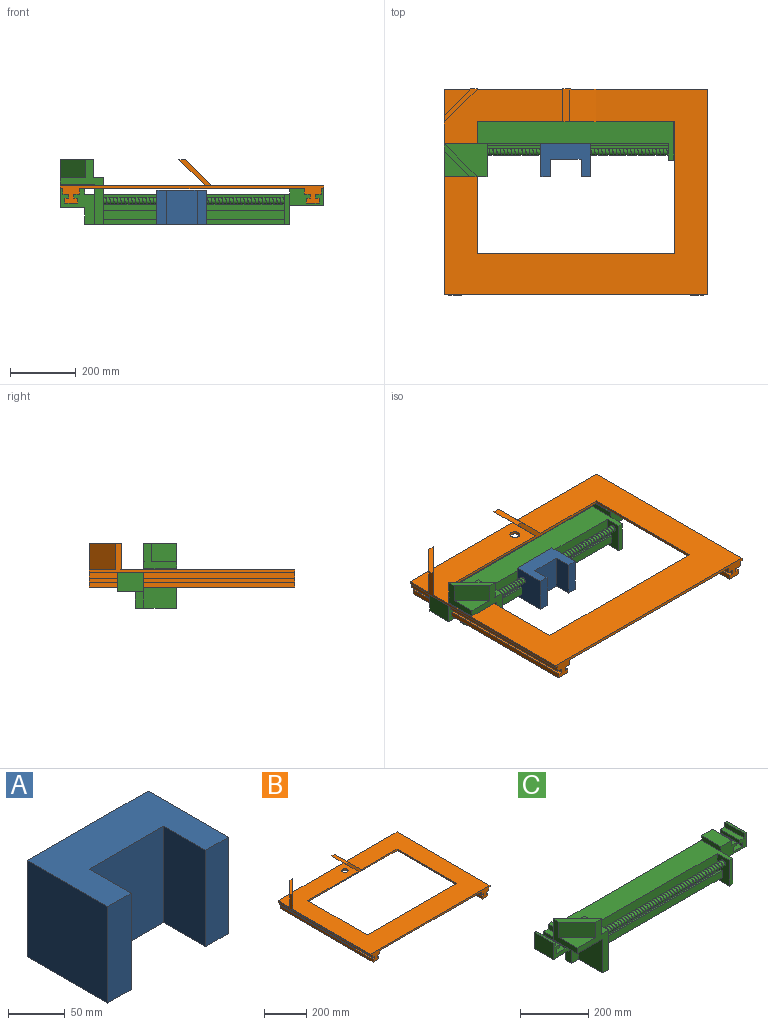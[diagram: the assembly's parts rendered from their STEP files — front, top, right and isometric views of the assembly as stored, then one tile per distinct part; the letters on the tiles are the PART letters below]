
ASSEMBLY  parts=3 mates=3
PART A: 10 faces, bbox 150x100x104 mm
  f0: plane 150x104mm, normal (0,1,0), area 15600mm2, adj f1,f7,f8,f9
  f1: plane 104x100mm, normal (1,0,0), area 10400mm2, adj f0,f2,f8,f9
  f2: plane 104x28.15mm, normal (0,-1,0), area 2927.1mm2, adj f1,f3,f8,f9
  f3: plane 104x52.39mm, normal (-1,0,0), area 5448.2mm2, adj f2,f4,f8,f9
  f4: plane 104x93.1mm, normal (0,-1,0), area 9682.7mm2, adj f3,f5,f8,f9
  f5: plane 104x52.39mm, normal (1,0,0), area 5448.2mm2, adj f4,f6,f8,f9
  f6: plane 104x28.75mm, normal (0,-1,0), area 2990.2mm2, adj f5,f7,f8,f9
  f7: plane 104x100mm, normal (-1,0,0), area 10400mm2, adj f0,f6,f8,f9
  f8: plane 150x100mm, normal (0,0,1), area 10122.7mm2, adj f0,f1,f2,f3,f4,f5,f6,f7
  f9: plane 150x100mm, normal (0,0,-1), area 10122.7mm2, adj f0,f1,f2,f3,f4,f5,f6,f7
PART B: 42 faces, bbox 800x625x132 mm
  f0: plane 625x7.98mm, normal (0,0,-1), area 4984.4mm2, adj f6,f8,f40,f41
  f1: plane 682.77x625mm, normal (0,0,-1), area 186024.3mm2, adj f3,f4,f5,f6,f9,f15,f29,f30
  f2: plane 800x625mm, normal (0,0,1), area 252293.1mm2, adj f3,f4,f5,f6,f7,f8,f9,f12
  f3: plane 600x88mm, normal (0,-1,0), area 6400mm2, adj f1,f2,f4,f9,f12,f13,f14
  f4: plane 400x8mm, normal (-1,0,0), area 3200mm2, adj f1,f2,f3,f5
  f5: plane 600x8mm, normal (0,1,0), area 4800mm2, adj f1,f2,f4,f9
  f6: plane 800x132mm, normal (0,1,0), area 12854.9mm2, adj f0,f1,f2,f7,f8,f10,f11,f12
  f7: plane 625x88mm, normal (-1,0,0), area 6600mm2, adj f2,f6,f10,f11,f16,f17,f18,f41
  f8: plane 625x8mm, normal (1,0,0), area 5000mm2, adj f0,f2,f6,f41
  f9: plane 400x8mm, normal (1,0,0), area 3200mm2, adj f1,f2,f3,f5
  f10: plane 80x80mm, normal (0,0,1), area 3200mm2, adj f6,f7,f16
  f11: plane 625x7.98mm, normal (0,0,-1), area 4984.4mm2, adj f6,f7,f19,f41
  f12: plane 100x80mm, normal (0.71,0,0.71), area 11313.7mm2, adj f2,f3,f6,f14
  f13: plane 100x80mm, normal (-0.71,0,-0.71), area 11313.7mm2, adj f2,f3,f6,f14
  f14: plane 100x20mm, normal (0,0,1), area 2000mm2, adj f3,f6,f12,f13
  f15: cylinder r=15mm len=30mm, axis (0,0,-1), area 754mm2, adj f1,f2
  f16: plane 80x80mm, normal (-0.71,0.71,0), area 9051mm2, adj f6,f7,f10,f18
  f17: plane 100x100mm, normal (0.71,-0.71,0), area 11313.7mm2, adj f2,f6,f7,f18
  f18: plane 100x100mm, normal (0,0,1), area 1800mm2, adj f6,f7,f16,f17
  f19: plane 625x17.11mm, normal (-1,0,0), area 10694.5mm2, adj f6,f11,f20,f41
  f20: plane 625x17.86mm, normal (0,0,-1), area 11162mm2, adj f6,f19,f21,f41
  f21: plane 625x12.04mm, normal (-1,0,0), area 7525mm2, adj f6,f20,f22,f41
  f22: plane 625x12.11mm, normal (0,0,1), area 7570.6mm2, adj f6,f21,f23,f41
  f23: plane 625x14.85mm, normal (-1,0,0), area 9280.6mm2, adj f6,f22,f24,f41
  f24: plane 625x39.15mm, normal (0,0,-1), area 24467.1mm2, adj f6,f23,f25,f41
  f25: plane 625x14.85mm, normal (1,0,0), area 9280.6mm2, adj f6,f24,f26,f41
  f26: plane 625x12.11mm, normal (0,0,1), area 7570.6mm2, adj f6,f25,f27,f41
  f27: plane 625x12.04mm, normal (1,0,0), area 7525mm2, adj f6,f26,f28,f41
  f28: plane 625x17.86mm, normal (0,0,-1), area 11162mm2, adj f6,f27,f29,f41
  f29: plane 625x17.11mm, normal (1,0,0), area 10694.5mm2, adj f1,f6,f28,f41
  f30: plane 625x17.11mm, normal (-1,0,0), area 10694.5mm2, adj f1,f6,f31,f41
  f31: plane 625x17.86mm, normal (0,0,-1), area 11162mm2, adj f6,f30,f32,f41
  f32: plane 625x12.04mm, normal (-1,0,0), area 7525mm2, adj f6,f31,f33,f41
  f33: plane 625x12.11mm, normal (0,0,1), area 7570.6mm2, adj f6,f32,f34,f41
  f34: plane 625x14.85mm, normal (-1,0,0), area 9280.6mm2, adj f6,f33,f35,f41
  f35: plane 625x39.15mm, normal (0,0,-1), area 24467.1mm2, adj f6,f34,f36,f41
  f36: plane 625x14.85mm, normal (1,0,0), area 9280.6mm2, adj f6,f35,f37,f41
  f37: plane 625x12.11mm, normal (0,0,1), area 7570.6mm2, adj f6,f36,f38,f41
  f38: plane 625x12.04mm, normal (1,0,0), area 7525mm2, adj f6,f37,f39,f41
  f39: plane 625x17.86mm, normal (0,0,-1), area 11162mm2, adj f6,f38,f40,f41
  f40: plane 625x17.11mm, normal (1,0,0), area 10694.5mm2, adj f0,f6,f39,f41
  f41: plane 800x52mm, normal (0,-1,0), area 9654.9mm2, adj f0,f1,f2,f7,f8,f11,f19,f20
PART C: 67 faces, bbox 800.3x180.3x197.3 mm
  f0: plane 679.93x109.16mm, normal (0,-1,0), area 14389.8mm2, adj f1,f22,f23,f24,f25,f26,f27,f28
  f1: plane 51.31x25mm, normal (-1,0,-0.01), area 1282.8mm2, adj f0,f2,f22,f66
  f2: plane 621.48x56.6mm, normal (0,1,0), area 33520.7mm2, adj f1,f3,f22,f66
  f3: plane 92.05x75mm, normal (1,0,0), area 6017.5mm2, adj f2,f4,f5,f22,f38,f66
  f4: plane 92.05x16.02mm, normal (0,-1,0), area 1475.1mm2, adj f3,f38,f65,f66
  f5: plane 104.04x52.56mm, normal (0,-1,0), area 3795.1mm2, adj f3,f6,f8,f9,f10,f11,f12,f13
  f6: plane 80x17.11mm, normal (-1,0,0), area 1368.9mm2, adj f5,f7,f8,f38
  f7: plane 800x58.49mm, normal (0,1,0), area 30168.5mm2, adj f6,f8,f9,f10,f11,f12,f13,f14
  f8: plane 80x45.43mm, normal (0,0,1), area 3634.2mm2, adj f5,f6,f7,f9
  f9: plane 80x17.11mm, normal (1,0,0), area 1368.9mm2, adj f5,f7,f8,f10
  f10: plane 80x17.86mm, normal (0,0,1), area 1428.7mm2, adj f5,f7,f9,f11
  f11: plane 80x12.04mm, normal (1,0,0), area 963.2mm2, adj f5,f7,f10,f12
  f12: plane 80x12.11mm, normal (0,0,-1), area 969mm2, adj f5,f7,f11,f13
  f13: plane 80x14.85mm, normal (1,0,0), area 1187.9mm2, adj f5,f7,f12,f14
  f14: plane 80x39.15mm, normal (0,0,1), area 3131.8mm2, adj f5,f7,f13,f15
  f15: plane 80x14.85mm, normal (-1,0,0), area 1187.9mm2, adj f5,f7,f14,f16
  f16: plane 80x12.11mm, normal (0,0,-1), area 969mm2, adj f5,f7,f15,f17
  f17: plane 80x12.04mm, normal (-1,0,0), area 963.2mm2, adj f5,f7,f16,f18
  f18: plane 80x17.86mm, normal (0,0,1), area 1428.7mm2, adj f5,f7,f17,f19
  f19: plane 80x17.11mm, normal (-1,0,0), area 1368.9mm2, adj f5,f7,f18,f20
  f20: plane 80x7.98mm, normal (0,0,1), area 638mm2, adj f5,f7,f19,f21
  f21: plane 80x51.68mm, normal (1,0,0), area 4134.1mm2, adj f5,f7,f20,f22
  f22: plane 800x80mm, normal (0.01,0,-1), area 48464.7mm2, adj f0,f1,f2,f3,f5,f7,f21,f23
  f23: plane 80x58.49mm, normal (-1,0,0), area 4678.9mm2, adj f0,f7,f22,f24
  f24: plane 80x7.98mm, normal (0,0,1), area 638mm2, adj f0,f7,f23,f25
  f25: plane 80x17.11mm, normal (1,0,0), area 1368.9mm2, adj f0,f7,f24,f26
  f26: plane 80x17.86mm, normal (0,0,1), area 1428.7mm2, adj f0,f7,f25,f27
  f27: plane 80x12.04mm, normal (1,0,0), area 963.2mm2, adj f0,f7,f26,f28
  f28: plane 80x12.11mm, normal (0,0,-1), area 969mm2, adj f0,f7,f27,f29
  f29: plane 80x14.85mm, normal (1,0,0), area 1187.9mm2, adj f0,f7,f28,f30
  f30: plane 80x39.15mm, normal (0,0,1), area 3131.8mm2, adj f0,f7,f29,f31
  f31: plane 80x14.85mm, normal (-1,0,0), area 1187.9mm2, adj f0,f7,f30,f32
  f32: plane 80x12.11mm, normal (0,0,-1), area 969mm2, adj f0,f7,f31,f33
  f33: plane 80x12.04mm, normal (-1,0,0), area 963.2mm2, adj f0,f7,f32,f34
  f34: plane 80x17.86mm, normal (0,0,1), area 1428.7mm2, adj f0,f7,f33,f35
  f35: plane 80x17.11mm, normal (-1,0,0), area 1368.9mm2, adj f0,f7,f34,f36
  f36: plane 80x15.37mm, normal (0,0,1), area 1229.4mm2, adj f0,f7,f35,f37
  f37: plane 80x17.11mm, normal (1,0,0.01), area 1368.9mm2, adj f0,f7,f36,f38
  f38: plane 621.83x130mm, normal (0,0,1), area 50547.5mm2, adj f0,f3,f4,f6,f7,f37,f39,f50
  f39: plane 550x50.09mm, normal (0,-1,0), area 27549.8mm2, adj f38,f40,f61,f65
  f40: plane 550x6.76mm, normal (0,0,1), area 3716.9mm2, adj f39,f41,f61,f65
  f41: plane 550x9.88mm, normal (0,-1,0), area 5436mm2, adj f40,f42,f61,f65
  f42: plane 550x7.79mm, normal (0,0,1), area 4283.9mm2, adj f41,f43,f61,f65
  f43: plane 550x9.88mm, normal (0,1,0), area 5436mm2, adj f42,f44,f61,f65
  f44: plane 550x6.03mm, normal (0,0,1), area 3317.9mm2, adj f43,f45,f61,f65
  f45: plane 550x25.8mm, normal (0,-1,0), area 14187.8mm2, adj f44,f46,f61,f65
  f46: plane 550x6.03mm, normal (0,0,-1), area 3317.9mm2, adj f45,f47,f61,f65
  f47: plane 550x9.88mm, normal (0,1,0), area 5436mm2, adj f46,f48,f61,f65
  f48: plane 550x7.79mm, normal (0,0,-1), area 4283.9mm2, adj f47,f49,f61,f65
  f49: plane 550x9.88mm, normal (0,-1,0), area 5436mm2, adj f48,f61,f64,f65
  f50: plane 130x50mm, normal (0,1,0), area 3350mm2, adj f38,f51,f57,f58,f59,f61
  f51: plane 130x100mm, normal (0,0,1), area 8000mm2, adj f50,f52,f56,f61
  f52: plane 196.66x130mm, normal (0,-1,0), area 6929.9mm2, adj f51,f53,f54,f55,f56,f57,f58,f59
  f53: plane 76.58x76.18mm, normal (0,0,1), area 2917mm2, adj f52,f54,f57
  f54: plane 76.58x76.18mm, normal (-0.71,-0.71,0), area 5941mm2, adj f52,f53,f55,f57
  f55: plane 100x100mm, normal (0,0,1), area 2083mm2, adj f52,f54,f56,f57
  f56: plane 100x100mm, normal (0.71,0.71,0), area 7778.2mm2, adj f51,f52,f55,f57
  f57: plane 100x75mm, normal (-1,0,0), area 3309.9mm2, adj f50,f52,f53,f54,f55,f56,f58
  f58: plane 105x100mm, normal (0,0,-1), area 10500mm2, adj f50,f52,f57,f59
  f59: plane 121.66x100mm, normal (-1,0,0), area 12166.4mm2, adj f0,f50,f52,f58,f60
  f60: plane 100x25mm, normal (0,0,-1), area 2500mm2, adj f0,f52,f59,f61
  f61: plane 141.94x100.27mm, normal (1,0,0), area 13476.9mm2, adj f0,f39,f40,f41,f42,f43,f44,f45
  f62: bspline ~550x20mm, area 6325.7mm2, adj f61,f63,f65
  f63: cylinder r=10mm len=550mm, axis (-1,0,0), area 33457.1mm2, adj f61,f62,f65
  f64: plane 550x6.76mm, normal (0,0,-1), area 3716.9mm2, adj f0,f49,f61,f65
  f65: plane 92.32x50.27mm, normal (-1,0,0), area 3913mm2, adj f0,f4,f38,f39,f40,f41,f42,f43
  f66: plane 621.05x75mm, normal (0,0,-1), area 16327.4mm2, adj f0,f1,f2,f3,f4,f65
PLACE A t=(-3.7,163.4,-35.81)mm
PLACE B t=(-1.95,-295.76,-35.81)mm fixed
PLACE C t=(-1.95,163.4,-35.81)mm
MATE planar A.f9 <-> C.f66  axis (0,0,-1) through (13.38,-209.22,-144.97)mm
MATE planar A.f0 <-> C.f0  axis (0,1,0) through (-33.48,-161.6,-92.97)mm
MATE slider C.f0 <-> B.f41  axis (0,-1,0) through (-349.09,-161.6,-79.81)mm
